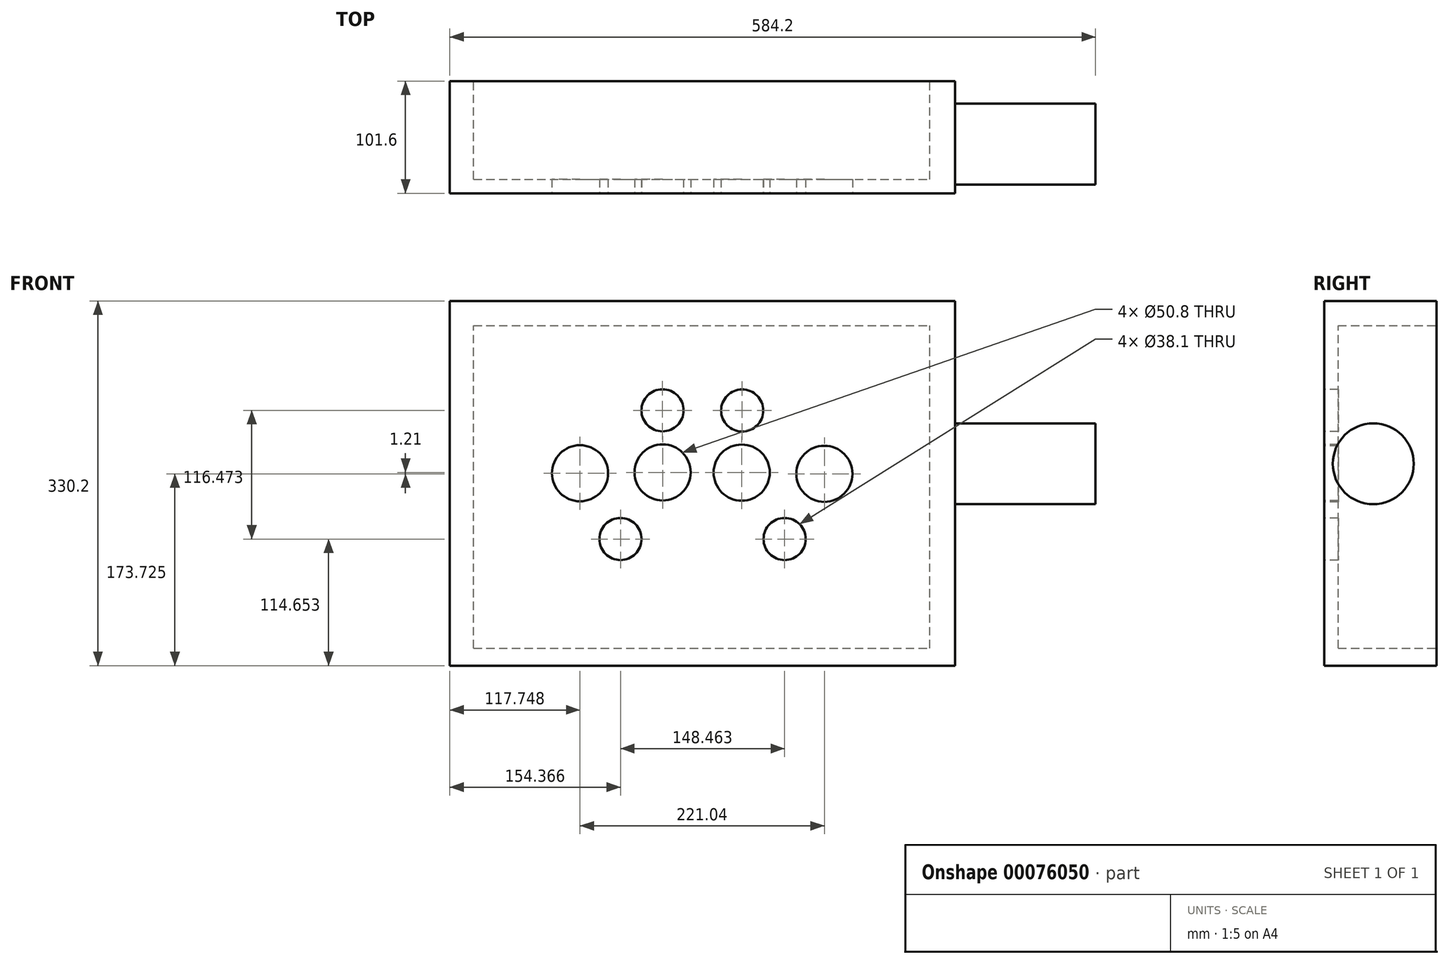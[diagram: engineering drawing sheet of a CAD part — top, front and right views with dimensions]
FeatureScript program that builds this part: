
annotation { "Feature Type Name" : "Feature", "Feature Type Description" : "" }
export const myFeature = defineFeature(function(context is Context, id is Id, definition is map)
    precondition{}
    {
        {
            var Q0;
            Q0=qCreatedBy(makeId("Front.planeOp"),FACE);
            var sketch = newSketch(context, id + "F0", { "sketchPlane" : qUnion([Q0])});
            skLineSegment(sketch, "E0.bottom", {"start": v(-227.9, 158.4) * mm, "end": v(229.3, 158.4) * mm});
            skLineSegment(sketch, "E0.top", {"start": v(-227.9, -171.8) * mm, "end": v(229.3, -171.8) * mm});
            skLineSegment(sketch, "E0.left", {"start": v(-227.9, 158.4) * mm, "end": v(-227.9, -171.8) * mm});
            skLineSegment(sketch, "E0.right", {"start": v(229.3, 158.4) * mm, "end": v(229.3, -171.8) * mm});
            skSolve(sketch);
        }
        {
            var Q0;
            Q0=makeQuery(id+"F0.imprint","IMPRINT",FACE,{"disambiguationData":[TD([[makeQuery(id+"F0.imprint","IMPRINT",EDGE,{"derivedFrom":sQuery(id+"F0.wireOp",EDGE,"E0.bottom")}),-1.0]])]});
            extrude(context, id + "F1", {"entities" : qUnion([Q0]), "depth" : 101.6 * mm});
        }
        {
            var Q0;
            Q0=makeQuery(id+"F1.opExtrude","CAP_FACE",FACE,{"disambiguationData":[OSD([sQuery(id+"F0.wireOp",EDGE,"E0.bottom"),sQuery(id+"F0.wireOp",EDGE,"E0.top"),sQuery(id+"F0.wireOp",EDGE,"E0.left"),sQuery(id+"F0.wireOp",EDGE,"E0.right")])],"isStart":true});
            var sketch = newSketch(context, id + "F2", { "sketchPlane" : qUnion([Q0])});
            skLineSegment(sketch, "E1.bottom", {"start": v(206.38, -155.93) * mm, "end": v(-206.37, -155.93) * mm});
            skLineSegment(sketch, "E1.top", {"start": v(206.38, 136.17) * mm, "end": v(-206.38, 136.17) * mm});
            skLineSegment(sketch, "E1.left", {"start": v(206.38, -155.93) * mm, "end": v(206.38, 136.17) * mm});
            skLineSegment(sketch, "E1.right", {"start": v(-206.37, -155.93) * mm, "end": v(-206.38, 136.17) * mm});
            skSolve(sketch);
        }
        {
            var Q0;
            Q0 = qSketchRegion(id + "F2", true);
            extrude(context, id + "F3", {"entities" : qUnion([Q0]), "operationType" : NewBodyOperationType.REMOVE, "oppositeDirection" : true, "depth" : 88.9 * mm});
        }
        {
            var Q0;
            Q0=makeQuery(id+"F1.opExtrude","CAP_FACE",FACE,{"disambiguationData":[OSD([sQuery(id+"F0.wireOp",EDGE,"E0.bottom"),sQuery(id+"F0.wireOp",EDGE,"E0.top"),sQuery(id+"F0.wireOp",EDGE,"E0.left"),sQuery(id+"F0.wireOp",EDGE,"E0.right")])],"isStart":false});
            var sketch = newSketch(context, id + "F4", { "sketchPlane" : qUnion([Q0])});
            skCircle(sketch, "E2", {"center": v(-35.4, 3.12) * mm, "radius": 25.4 * mm});
            skCircle(sketch, "E3", {"center": v(-110.15, 2.38) * mm, "radius": 25.4 * mm});
            skCircle(sketch, "E4", {"center": v(-35.55, 59.32) * mm, "radius": 19.05 * mm});
            skCircle(sketch, "E5", {"center": v(-73.53, -57.16) * mm, "radius": 19.05 * mm});
            skCircle(sketch, "E6.MirrorC", {"center": v(36.53, 59.16) * mm, "radius": 19.05 * mm});
            skCircle(sketch, "E7.MirrorC", {"center": v(110.89, 1.92) * mm, "radius": 25.4 * mm});
            skCircle(sketch, "E8.MirrorC", {"center": v(36.14, 2.97) * mm, "radius": 25.4 * mm});
            skLineSegment(sketch, "E9", {"start": v(0.7, 158.4) * mm, "end": v(0.7, -171.8) * mm});
            skCircle(sketch, "E10.MirrorC", {"center": v(74.93, -57.16) * mm, "radius": 19.05 * mm});
            skSolve(sketch);
        }
        {
            var Q0;
            Q0 = qSketchRegion(id + "F4", true);
            extrude(context, id + "F5", {"entities" : qUnion([Q0]), "operationType" : NewBodyOperationType.REMOVE, "endBound" : BoundingType.UP_TO_NEXT, "oppositeDirection" : true, "depth" : 25.4 * mm});
        }
        {
            var Q0;
            Q0=makeQuery(id+"F1.opExtrude","SWEPT_FACE",FACE,{"disambiguationData":[OSD([sQuery(id+"F0.wireOp",EDGE,"E0.right")])]});
            var sketch = newSketch(context, id + "F6", { "sketchPlane" : qUnion([Q0])});
            skCircle(sketch, "E11", {"center": v(-57.18, 10.97) * mm, "radius": 36.62 * mm});
            skSolve(sketch);
        }
        {
            var Q0;
            Q0=makeQuery(id+"F6.imprint","IMPRINT",FACE,{"disambiguationData":[TD([[makeQuery(id+"F6.imprint","IMPRINT",EDGE,{"derivedFrom":sQuery(id+"F6.wireOp",EDGE,"E11")}),1.0]])]});
            extrude(context, id + "F7", {"entities" : qUnion([Q0]), "operationType" : NewBodyOperationType.ADD, "depth" : 127 * mm});
        }
    });
